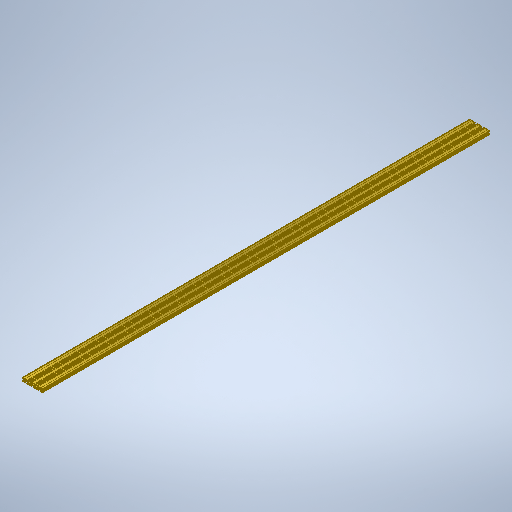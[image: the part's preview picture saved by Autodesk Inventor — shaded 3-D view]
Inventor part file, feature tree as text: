
AUTODESK INVENTOR PART (.ipt)
format: ipt  version: 2025.2 (Build 292293000, 293)  size: 528,384 bytes
history: native  units: mm
features: other x1, extrude x1, mirror x1, sketch x1
ambient origin geometry x8: Origin, YZ Plane, XZ Plane, XY Plane, X Axis, Y Axis, Z Axis, Center Point
bodies: Body1 (feature_tree)
feature tree (4):
  other  "Sólido1"
  extrude  "Extrusão1"  Depth=15.0mm
  mirror  "Espelhar1"
  sketch  "Esboço1"  dims[d0=90.0mm d5=15.0mm d6=5.5mm d7=6.2mm d9=1.5mm d10=3.0mm d24=0.5mm d74=8.2mm d75=30.0mm d76=15.0mm d79=2.2mm d81=2.2mm d86=0.5mm d87=2.2mm d88=2.2mm d90=2000.0mm d91=0.0mm d93=2.2mm]
